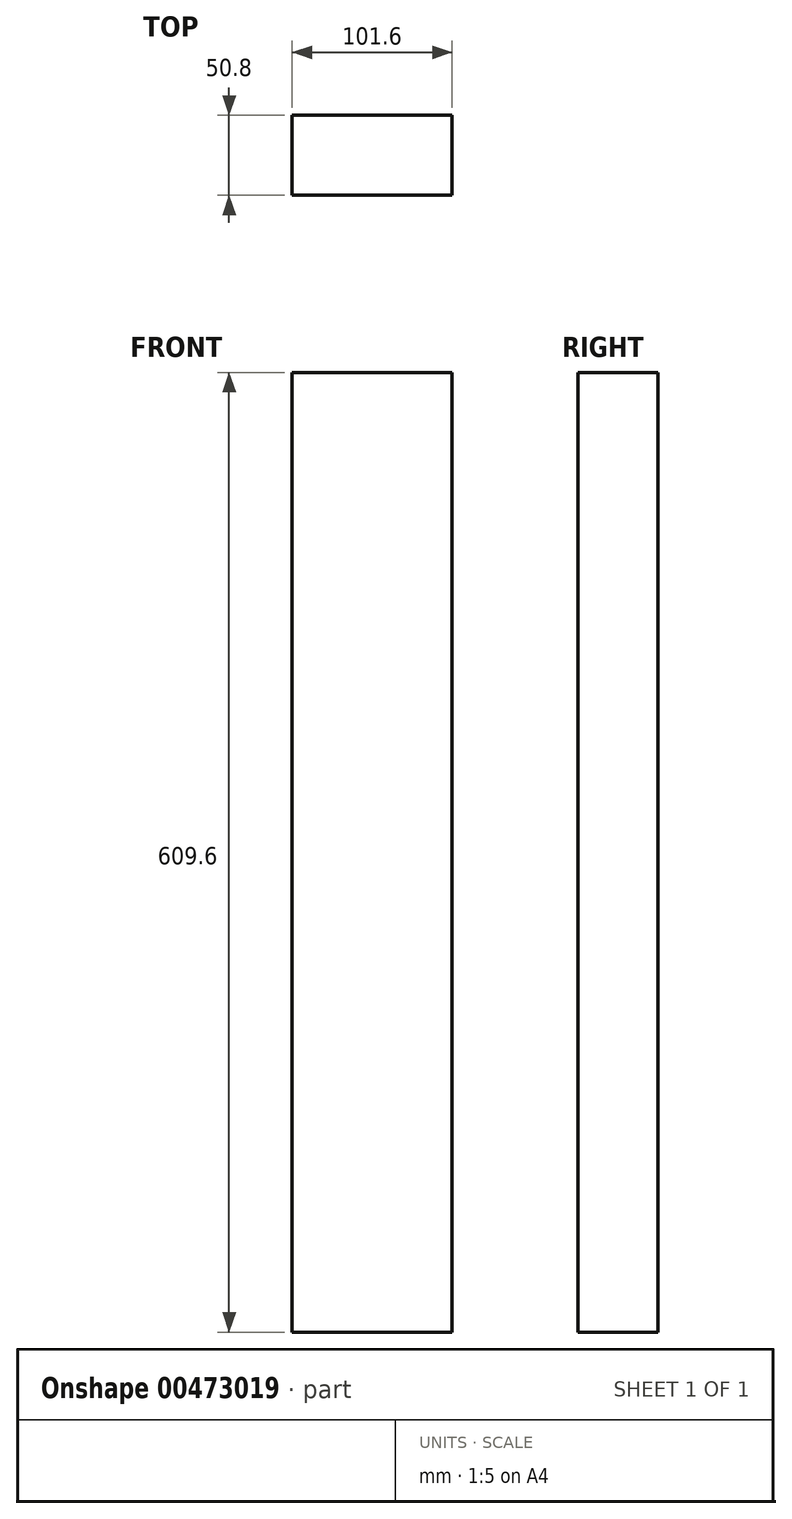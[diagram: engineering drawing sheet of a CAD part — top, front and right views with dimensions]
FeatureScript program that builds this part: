
annotation { "Feature Type Name" : "Feature", "Feature Type Description" : "" }
export const myFeature = defineFeature(function(context is Context, id is Id, definition is map)
    precondition{}
    {
        {
            var Q0;
            Q0=qCreatedBy(makeId("Top.planeOp"),FACE);
            var sketch = newSketch(context, id + "F0", { "sketchPlane" : qUnion([Q0])});
            skLineSegment(sketch, "E0.bottom", {"start": v(50.8, 25.4) * mm, "end": v(-50.8, 25.4) * mm});
            skLineSegment(sketch, "E0.top", {"start": v(50.8, -25.4) * mm, "end": v(-50.8, -25.4) * mm});
            skLineSegment(sketch, "E0.left", {"start": v(50.8, 25.4) * mm, "end": v(50.8, -25.4) * mm});
            skLineSegment(sketch, "E0.right", {"start": v(-50.8, 25.4) * mm, "end": v(-50.8, -25.4) * mm});
            skPoint(sketch, "E0.middle", {"position": v(0, 0) * mm});
            skSolve(sketch);
        }
        {
            var Q0;
            Q0 = qSketchRegion(id + "F0", true);
            extrude(context, id + "F1", {"entities" : qUnion([Q0]), "depth" : 609.6 * mm, "offsetDistance" : 25.4 * mm});
        }
    });
